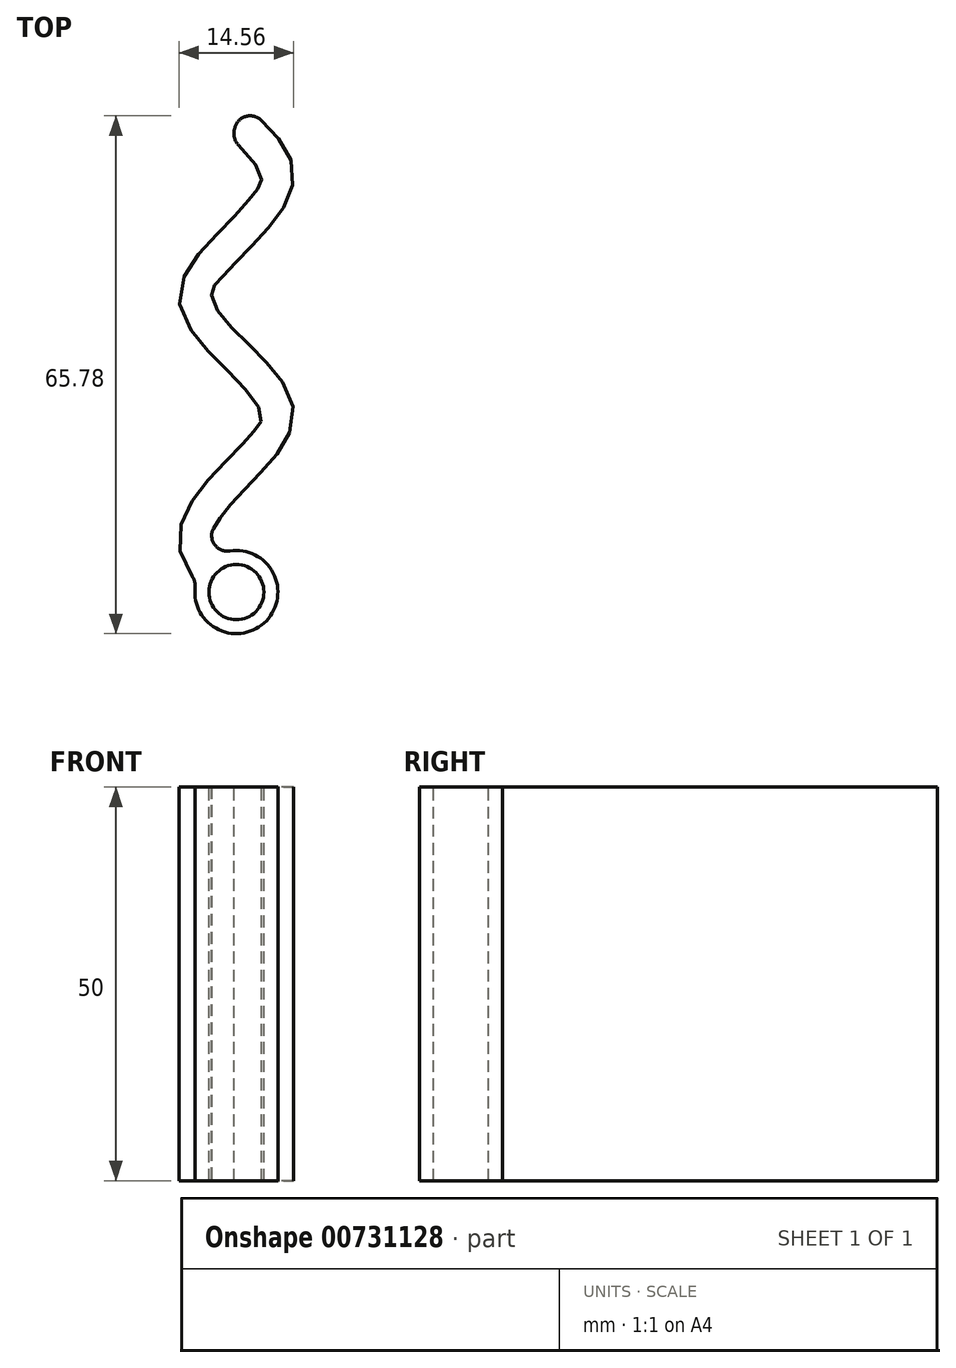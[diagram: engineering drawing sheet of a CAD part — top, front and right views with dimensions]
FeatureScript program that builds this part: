
annotation { "Feature Type Name" : "Feature", "Feature Type Description" : "" }
export const myFeature = defineFeature(function(context is Context, id is Id, definition is map)
    precondition{}
    {
        {
            var Q0;
            Q0=qCreatedBy(makeId("Top.planeOp"),FACE);
            var sketch = newSketch(context, id + "F0", { "sketchPlane" : qUnion([Q0])});
            skFitSpline(sketch, "E0", {"points": [v(0, -30) * mm, v(-5, -22.5) * mm, v(0, -15) * mm, v(5, -7.5) * mm, v(0, 0) * mm, v(-5, 7.5) * mm, v(0, 15) * mm, v(5, 22.5) * mm, v(0, 30) * mm], "startDerivative": vector(-96.66, 61.25) * mm, "endDerivative": vector(-77.33, 72.93) * mm});
            skSolve(sketch);
        }
        {
            var Q0;
            Q0=qCreatedBy(makeId("Right.planeOp"),FACE);
            var sketch = newSketch(context, id + "F1", { "sketchPlane" : qUnion([Q0])});
            skLineSegment(sketch, "E1.bottom", {"start": v(-32.5, 50) * mm, "end": v(-27.5, 50) * mm});
            skLineSegment(sketch, "E1.top", {"start": v(-32.5, 0) * mm, "end": v(-27.5, 0) * mm});
            skLineSegment(sketch, "E1.left", {"start": v(-32.5, 50) * mm, "end": v(-32.5, 0) * mm});
            skLineSegment(sketch, "E1.right", {"start": v(-27.5, 50) * mm, "end": v(-27.5, 0) * mm});
            skSolve(sketch);
        }
        {
            var Q0;
            Q0 = qSketchRegion(id + "F1", true);
            var Q1;
            Q1 = qConstructionFilter(qBodyType(qCreatedBy(id + "F0" ,EDGE), BodyType.WIRE), ConstructionObject.NO);
            sweep(context, id + "F2", {"profiles" : qUnion([Q0]), "path" : qUnion([Q1])});
        }
        {
            var Q0;
            Q0=makeQuery(id+"F2.opSweep","SWEPT_FACE",FACE,{"disambiguationData":[OSD([sQuery(id+"F0.wireOp",EDGE,"E0"),sQuery(id+"F1.wireOp",EDGE,"E1.bottom")])]});
            var sketch = newSketch(context, id + "F3", { "sketchPlane" : qUnion([Q0])});
            skCircle(sketch, "E2", {"center": v(0, -30) * mm, "radius": 5.27 * mm});
            skSolve(sketch);
        }
        {
            var Q0;
            Q0 = qSketchRegion(id + "F3", true);
            var Q1;
            Q1=makeQuery(id+"F2.opSweep","SWEPT_FACE",FACE,{"disambiguationData":[OSD([sQuery(id+"F0.wireOp",EDGE,"E0"),sQuery(id+"F1.wireOp",EDGE,"E1.top")])]});
            extrude(context, id + "F4", {"entities" : qUnion([Q0]), "operationType" : NewBodyOperationType.ADD, "endBound" : BoundingType.UP_TO_SURFACE, "oppositeDirection" : true, "depth" : 25 * mm, "endBoundEntityFace" : qUnion([Q1]), "offsetDistance" : 25 * mm});
        }
        {
            var Q0;
            Q0=sQuery(id+"F3.wireOp",VERTEX,"E2.center");
            var Q1;
            Q1=makeQuery(id+"F2.opSweep","SWEPT_BODY",BODY,{"disambiguationData":[OSD([sQuery(id+"F0.wireOp",EDGE,"E0"),sQuery(id+"F1.wireOp",EDGE,"E1.bottom"),sQuery(id+"F1.wireOp",EDGE,"E1.top"),sQuery(id+"F1.wireOp",EDGE,"E1.left"),sQuery(id+"F1.wireOp",EDGE,"E1.right")])]});
            hole(context, id + "F5", {"style" : HoleStyle.SIMPLE, "endStyle" : HoleEndStyle.THROUGH, "holeDiameter" : 7 * mm, "majorDiameter" : 5 * mm, "isTappedThrough" : true, "tappedDepth" : 10 * mm, "tapClearance" : 3, "startFromSketch" : true, "locations" : qUnion([Q0]), "scope" : qUnion([Q1])});
        }
        {
            var Q0;
            Q0=makeQuery(id+"F2.opSweep","CAP_EDGE",EDGE,{"disambiguationData":[OSD([sQuery(id+"F0.wireOp",VERTEX,"E0.end"),sQuery(id+"F1.wireOp",EDGE,"E1.right")])],"isStart":false});
            var Q1;
            Q1=makeQuery(id+"F2.opSweep","CAP_EDGE",EDGE,{"disambiguationData":[OSD([sQuery(id+"F0.wireOp",VERTEX,"E0.end"),sQuery(id+"F1.wireOp",EDGE,"E1.left")])],"isStart":false});
            var Q2;
            Q2=makeQuery(id+"F4.boolean.opBoolean","INTERSECT",EDGE,{"derivedFrom":[makeQuery(id+"F2.opSweep","SWEPT_FACE",FACE,{"disambiguationData":[OSD([sQuery(id+"F0.wireOp",EDGE,"E0"),sQuery(id+"F1.wireOp",EDGE,"E1.left")])]}),makeQuery(id+"F4.opExtrude","SWEPT_FACE",FACE,{"disambiguationData":[OSD([sQuery(id+"F3.wireOp",EDGE,"E2")])]})]});
            var Q3;
            Q3=makeQuery(id+"F4.boolean.opBoolean","INTERSECT",EDGE,{"derivedFrom":[makeQuery(id+"F2.opSweep","SWEPT_FACE",FACE,{"disambiguationData":[OSD([sQuery(id+"F0.wireOp",EDGE,"E0"),sQuery(id+"F1.wireOp",EDGE,"E1.right")])]}),makeQuery(id+"F4.opExtrude","SWEPT_FACE",FACE,{"disambiguationData":[OSD([sQuery(id+"F3.wireOp",EDGE,"E2")])]})]});
            fillet(context, id + "F6", {"entities" : qUnion([Q0, Q1, Q2, Q3]), "radius" : 2 * mm, "tangentPropagation" : true, "allowEdgeOverflow" : false});
        }
    });
